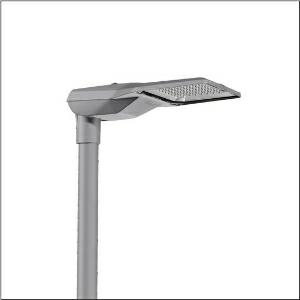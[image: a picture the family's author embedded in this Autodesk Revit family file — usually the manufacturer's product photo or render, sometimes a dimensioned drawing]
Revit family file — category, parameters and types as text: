
# Revit family: streetlight_sl_21_midi___st1_0a_5xe3d43s08lb_ab8b
name_source: partatom
category: Lighting Fixtures
units: mm (PartAtom-declared; Revit-internal decimal feet)

## family parameters
Cut with Voids When Loaded = No
Host = Face
Light Source = No
Part Type = Normal
Room Calculation Point = No
Round Connector Dimension = Use Diameter
Shared = No

## types (1)
- --- (1 x LED, 14950 lm, 99.6 W, 4000K)
    Apparent Load = 100 VA
    CIE Flux Codes = 37 72 97 100 100
    Color Rendering = 70
    Color Temperature = 4000K
    Default Elevation = 1800 mm
    Description = Streetlight SL 21 midi, mast luminaire, primary light control with lens, of PMMA, primary optical cover: cover, of toughened safety glass, transparent, light distribution: ST1.0a, light emission: direct distribution, primary light characteristic: asymmetric, installation type: side-entry, post-top, LED, High Power LED, rated luminous flux: 14.950lm, luminous efficacy: 150lm/W, light colour: 740, colour temperature: 4000K, control gear: D4i, control: overheat protection, constant luminous flux control, time-dependent luminous flux control, flexible luminous flux parameterisation, pre-setting: logarithmic dimming characteristic, mains connection: 230..240V, AC, 50/60Hz, start of lifetime: 100W, end of service life: 102W, reduction: 46W, luminaire housing, of diecast aluminium, powder-coated, Siteco® metallic grey (DB 702S), corrosivity category C5 mid according to DIN EN ISO 12944, please order mast flange separately, inclination adjustable: 0°, 5°, 10°, 15°, sealing non-destructively replaceable, multi-level sealing system, length: 644mm, width: 335mm, height: 110mm, mast flange for spigot size: 42mm (side-entry): 5XC10008XM4, 60/48mm (side-entry/post-top): 5XC10108XM2, 76/60mm (side-entry/post-top): 5XC10108XM1, mounting height: 4..8m, Smart Interface above, protection rating (complete): IP66, insulation class (complete): insulation class II (safety insulation), certification: CE, ENEC, ENEC+, VDE, impact resistance: IK10, permissible operating ambient temperature for outdoor applications: -40..+50°C, standard-compliant lighting for roads and squares, packaging unit: 1 piece

Light Distribution: ST1.0a
    Height = 111 mm
    Lamp = 1 x LED
    Lamp Light Flux = 14950 lm
    Lamp Power = 99.6 W
    Lamp count = 1
    Length = 644 mm
    Luminous efficacy = 150 lm/W
    Manufacturer = Siteco
    ModVariant = No
    Model = 5XE3D43S08LB
    Number of Poles = 1
    OnlyDefault = Yes
    Power Factor = 1
    Product Name = Streetlight SL 21 midi | ST1.0a
    Product group = mast luminaire | pylon top
    ProductGroupID = 6100
    Protection Class = Protection class II
    Protection Degree = IP 66
    RLX_Detail_Level = 1
    RLX_Emergency_Light_Flux = 0 lm
    RLX_Emergency_Type = 0
    RLX_Emergency_Type_DB = No
    RlxData = <blob elided: 26709 chars, md5=87619369>
    Socket = socket
    Standby Power = 0 W
    System Light Flux = 14950 lm
    System Power = 100 W
    Type Comments = factory setting: luminous flux: 100 % | dim-lin: 254 | 1020 mA
    Type Image = l_1004302.jpg
    URL = http://relux.com
    VarID = @adj_032123
    Voltage = 0 V
    Weight = 0.00 kg
    Width = 336 mm

## geometry (parser evidence)
native form markers: Blend x4, Sweep x9
no freeform markers — native parametric forms only
